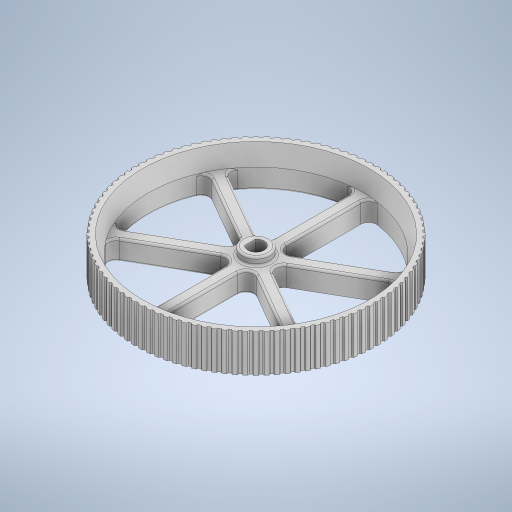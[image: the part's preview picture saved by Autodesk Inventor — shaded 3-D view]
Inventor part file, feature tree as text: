
AUTODESK INVENTOR PART (.ipt)
format: ipt  version: 2024.2 (Build 282272000, 272)  size: 1,017,856 bytes
history: native  units: mm
features: sketch x3, extrude x3, fillet x2, revolve x1
ambient origin geometry x8: Origin, YZ Plane, XZ Plane, XY Plane, X Axis, Y Axis, Z Axis, Center Point
bodies: Solid1 (feature_tree)
feature tree (9):
  revolve  "Revolution1"  [1 undecoded]
  sketch  "Sketch3"  dims[d3=30.0mm d4=360.0deg]
  extrude  "Extrusion1"  TaperAngle=360.0deg  [1 undecoded]
  extrude  "Extrusion2"  Depth=0.5mm
  extrude  "Extrusion3"  Depth=0.5mm
  fillet  "Fillet1"  Radius=7.0mm
  fillet  "Fillet2"  Radius=3.0mm
  sketch  "Sketch2"  dims[d0=3.0mm d2=5.0mm]
  sketch  "Sketch4"  dims[d5=4.1mm d6=1.5mm d7=15.0mm d8=7.0mm d9=3.0mm d10=1.5mm d11=60.0mm d13=360.0deg d15=5.0mm d16=0.0mm d17=7.0mm d18=0.0mm d19=120.0deg d20=120.0deg d21=1.6mm d22=1.0mm d23=0.5mm d24=1000.0mm d26=360.0deg d28=0.0mm d29=0.0mm d30=2.0mm d31=0.5mm d37=1.5mm d38=9.5mm d32=0.0mm d33=0.0mm d34=0.0mm d35=0.0mm]
note: 2 required parameter values undecoded (feature->parameter linkage not recoverable at this tier; creation-order binding heuristic only, values carry confidence <= 0.55)